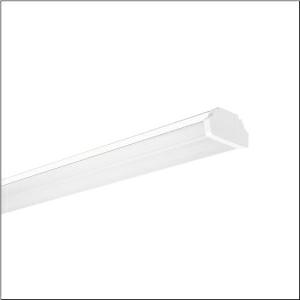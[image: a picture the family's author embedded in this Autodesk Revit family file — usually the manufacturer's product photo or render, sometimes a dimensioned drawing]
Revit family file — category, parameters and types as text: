
# Revit family: dus_31_gen_2_53bd812cv475c2_3345
name_source: partatom
category: Lighting Fixtures
units: mm (PartAtom-declared; Revit-internal decimal feet)

## family parameters
Cut with Voids When Loaded = No
Host = Face
Light Source = No
Part Type = Normal
Room Calculation Point = No
Round Connector Dimension = Use Diameter
Shared = No

## types (1)
- --- (1 x LED, 7600 lm, 40.5 W, 4000K)
    Apparent Load = 41 VA
    CIE Flux Codes = 47 80 95 93 100
    Color Rendering = 80
    Color Temperature = 4000K
    Default Elevation = 1800 mm
    Description = DUS 31 Gen.2, luminaire insert, of sheet steel, coil coated, white, length: 1.535mm, width: 81mm, height: 90mm, 5x system unit, system units: 307mm, LED rated luminous flux: 7.600lm, light colour: 840, SDCM (Standard Deviation of Colour Matching)MacAdam ≤ 3 SDCM (initial), control gear: ON/OFF Multilumen, CLOi, with plug, 3-pole, with phase selection, mains connection: 220..240V, AC, 50/60Hz, start of lifetime: 41W, end of service life: 48W, through-wiring accessed according to module size, primary optical cover: cover, of PMMA, light emission: direct distribution, primary light characteristic: symmetric, protection rating (complete): IP20, protection rating (LED compartment): IP50, insulation class (complete): insulation class I (protective earthing), certification: CE, ENEC, VDE, UKCA, impact resistance: IK03, permissible ambient temperature for indoor applications: -35..+50°C, corresponds to IFS (International Featured Standards) requirements for safety and quality in the food industry, reducing of maximum allowable ambient temperature of 5°C with ceiling mounting, packaging unit: 1 piece
    Height = 95 mm
    Lamp = 1 x LED
    Lamp Light Flux = 7600 lm
    Lamp Power = 40.5 W
    Lamp count = 1
    Length = 1535 mm
    Luminous efficacy = 188 lm/W
    Manufacturer = Siteco
    ModVariant = No
    Model = 53BD812CV475C2
    Mounting Place = Ceiling
    Mounting Type = Pendant
    Number of Poles = 1
    OnlyDefault = Yes
    Power Factor = 1
    Product Name = DUS 31 Gen.2
    Product group = luminaire insert | ceiling pendant
    ProductGroupID = 901
    Protection Class = Protection class I
    Protection Degree = IP 20
    RLX_Detail_Level = 1
    RLX_Emergency_Light_Flux = 0 lm
    RLX_Emergency_Type = 0
    RLX_Emergency_Type_DB = No
    RlxData = <blob elided: 29857 chars, md5=4b9da9d0>
    Socket = socket
    Standby Power = 0 W
    System Light Flux = 7600 lm
    System Power = 41 W
    Type Comments = factory setting: luminous flux: 100 % | (A | C | E) | 94 mA
    Type Image = l_1319596.jpg
    URL = http://relux.com
    VarID = @adj_042381
    Voltage = 0 V
    Weight = 0.00 kg
    Width = 81 mm

## geometry (parser evidence)
native form markers: Blend x4, Sweep x11
no freeform markers — native parametric forms only
